# Revit family: 318_27545864294c44138141c1e3b364fa
name_source: partatom
category: Pipe Accessories
units: mm (PartAtom-declared; Revit-internal decimal feet)

## family parameters
Always vertical = Yes
Cut with Voids When Loaded = No
Part Type = Valve - Normal
Round Connector Dimension = Use Diameter
Shared = No
Work Plane-Based = No

## types (1)
- FAR-3906 1
    B = 36 mm  [stored 0.11811 ft]
    B1 = 12 mm  [stored 0.0393701 ft]
    B1__ve = -12 mm  [stored -0.0393701 ft]
    B2 = 24 mm  [stored 0.0787402 ft]
    B2__ve = -24 mm  [stored -0.0787402 ft]
    BP = 20 mm
    C = 45 mm  [stored 0.147638 ft]
    C1 = 23 mm
    CAT0 = Yes
    CenSd_R_6 = 18 mm
    Description = MULTIFAR 1" chr. lockshield manifold m-f, 4 ports m24x19
    E1 = 22 mm  [stored 0.0721785 ft]
    E1__ve = -22 mm  [stored -0.0721785 ft]
    E2 = 4 mm  [stored 0.0131234 ft]
    E2__ve = -4 mm  [stored -0.0131234 ft]
    E3 = 14 mm  [stored 0.0459318 ft]
    E3__ve = -14 mm  [stored -0.0459318 ft]
    L = 188 mm  [stored 0.616798 ft]
    L1 = 23 mm
    L1__ve = -23 mm
    L2 = 6 mm  [stored 0.019685 ft]
    L3 = 159 mm
    L3__ve = -159 mm
    L4 = 10 mm  [stored 0.0328084 ft]
    L4__ve = -10 mm  [stored -0.0328084 ft]
    L5 = 80 mm
    MP1 = 25 mm
    MP2 = 25 mm
    Manufacturer = FAR
    QmdConnectorList = 301;MP1;302;MP2;303;BP;304;BP;305;BP;306;BP
    R = 21 mm  [stored 0.0688976 ft]
    R1 = 13 mm
    R10 = 14 mm  [stored 0.0459318 ft]
    R11 = 14 mm  [stored 0.0459318 ft]
    R13 = 14 mm  [stored 0.0459318 ft]
    R3 = 17 mm
    R4 = 10 mm  [stored 0.0328084 ft]
    R6 = 11 mm  [stored 0.0360892 ft]
    R8 = 12 mm  [stored 0.0393701 ft]
    URL = www.far.eu
    magiPartTypeId = 318
    magiProductCode = FAR-3906 1
    magiProductFamilyId = 27545864294c44138141c1e3b364fa
    magiProductId = 27545864294c44138141c1e3b364fa

note: [stored X ft] marks values corroborated as IEEE doubles in the binary element streams (Revit-internal decimal feet)

## geometry (parser evidence)
native form markers: Sweep x3
no freeform markers — native parametric forms only
